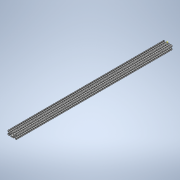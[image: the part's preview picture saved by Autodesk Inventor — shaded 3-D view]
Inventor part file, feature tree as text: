
AUTODESK INVENTOR PART (.ipt)
format: ipt  version: 2020 (Build 240168000, 168)  size: 343,552 bytes
history: native  units: in
note: dims shown in document units (in); Inventor stores cm internally (conversion verified against a paired STEP export)
features: sketch x2, extrude x1
ambient origin geometry x8: Origin, YZ Plane, XZ Plane, XY Plane, X Axis, Y Axis, Z Axis, Center Point
bodies: Solid1 (feature_tree)
feature tree (3):
  extrude  "Extrusion1"  [1 undecoded]
  sketch  "Sketch2"
  sketch  "Sketch1"  dims[d0=35.0in d1=0.0in]
note: 1 required parameter value undecoded (feature->parameter linkage not recoverable at this tier; creation-order binding heuristic only, values carry confidence <= 0.55)
